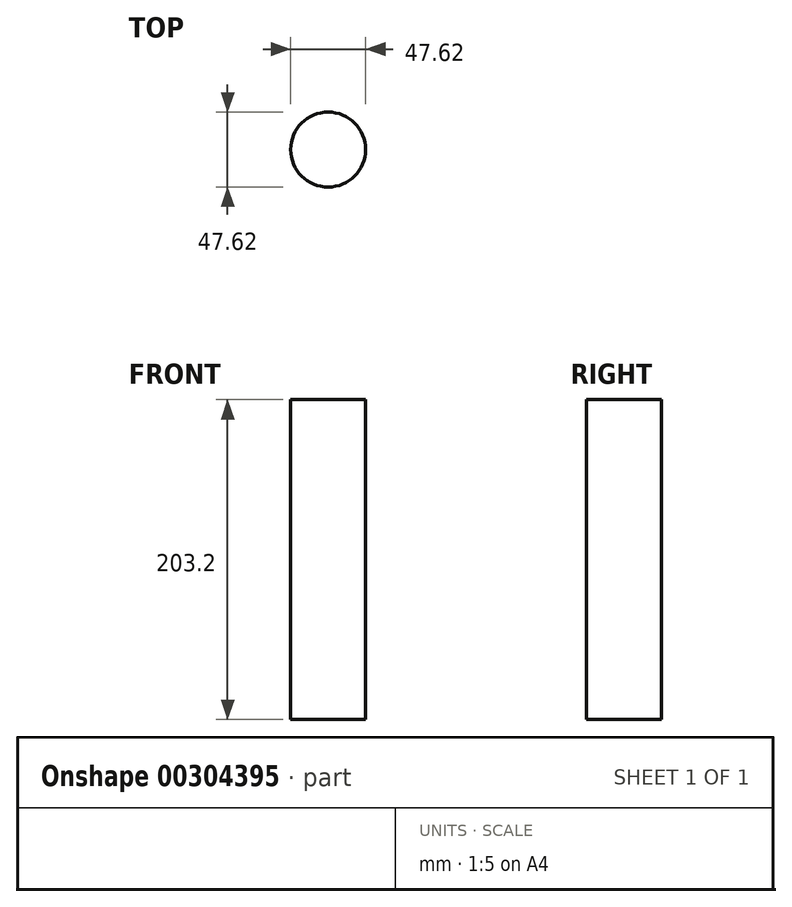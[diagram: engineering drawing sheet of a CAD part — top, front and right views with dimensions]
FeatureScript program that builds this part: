
annotation { "Feature Type Name" : "Feature", "Feature Type Description" : "" }
export const myFeature = defineFeature(function(context is Context, id is Id, definition is map)
    precondition{}
    {
        {
            var Q0;
            Q0=qCreatedBy(makeId("Top.planeOp"),FACE);
            var sketch = newSketch(context, id + "F0", { "sketchPlane" : qUnion([Q0])});
            skCircle(sketch, "E0", {"center": v(0, 0) * mm, "radius": 23.81 * mm});
            skSolve(sketch);
        }
        {
            var Q0;
            Q0=makeQuery(id+"F0.imprint","IMPRINT",FACE,{"disambiguationData":[TD([[makeQuery(id+"F0.imprint","IMPRINT",EDGE,{"derivedFrom":sQuery(id+"F0.wireOp",EDGE,"E0")}),1.0]])]});
            extrude(context, id + "F1", {"entities" : qUnion([Q0]), "endBound" : BoundingType.SYMMETRIC, "depth" : 203.2 * mm, "offsetDistance" : 25.4 * mm});
        }
    });
